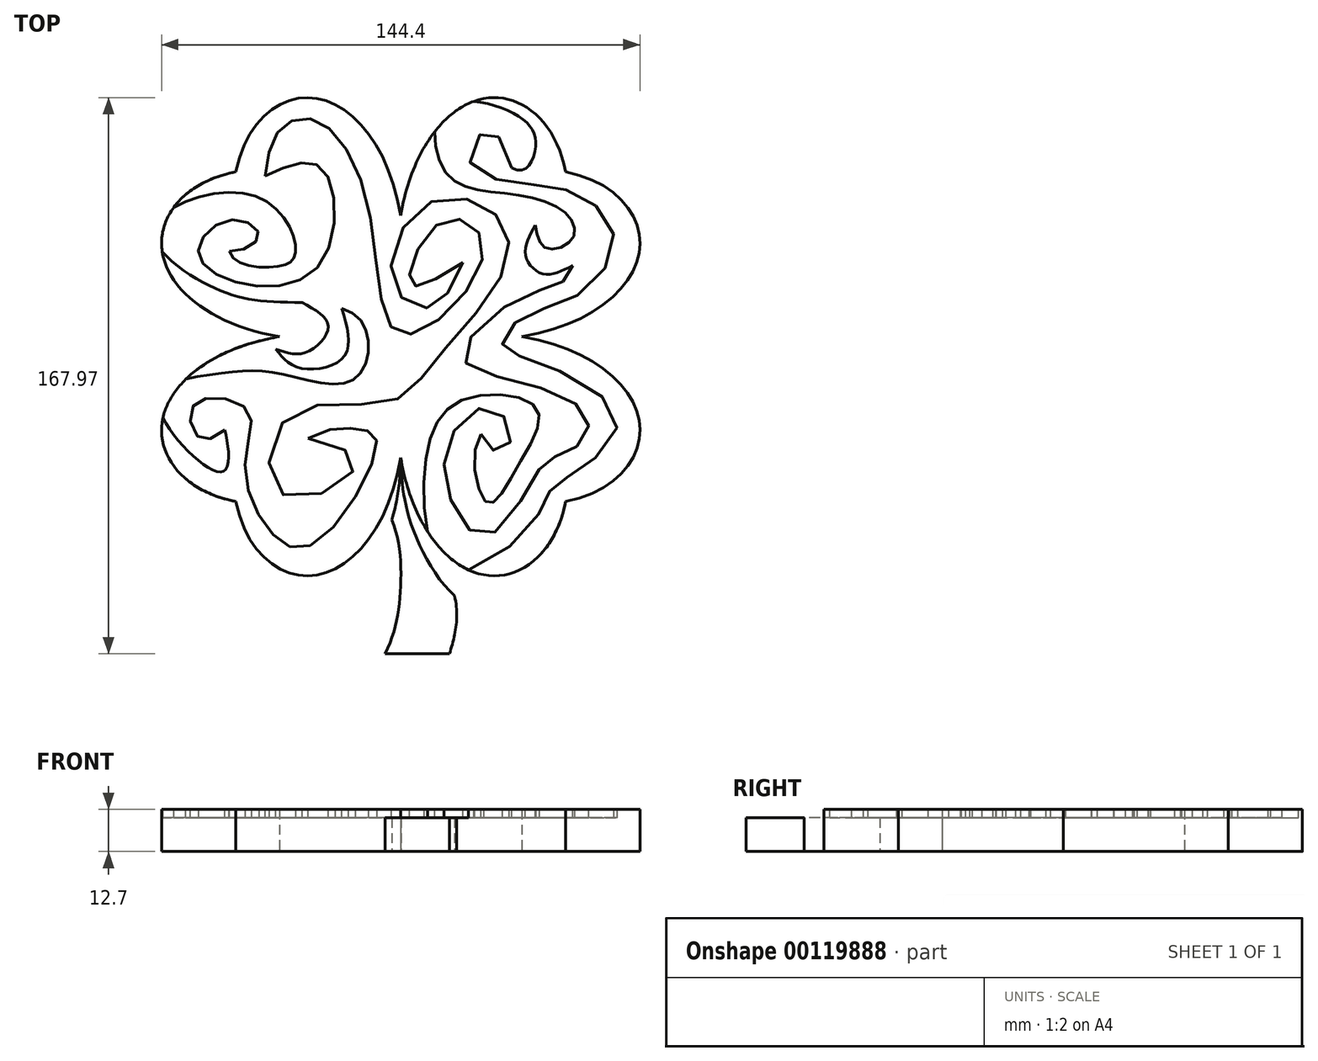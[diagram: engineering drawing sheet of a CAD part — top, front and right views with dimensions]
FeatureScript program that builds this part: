
annotation { "Feature Type Name" : "Feature", "Feature Type Description" : "" }
export const myFeature = defineFeature(function(context is Context, id is Id, definition is map)
    precondition{}
    {
        {
            var Q0;
            Q0=qCreatedBy(makeId("Top.planeOp"),FACE);
            var sketch = newSketch(context, id + "F0", { "sketchPlane" : qUnion([Q0])});
            skLineSegment(sketch, "E0", {"start": v(0, 0) * mm, "end": v(-53.24, 53.24) * mm, "construction": true});
            skFitSpline(sketch, "E1", {"points": [v(-36.57, 0) * mm, v(-72.1, 26.37) * mm, v(-49.78, 49.78) * mm], "startDerivative": vector(-116.66, 19.41) * mm, "endDerivative": vector(102.08, 20.22) * mm});
            skLineSegment(sketch, "E2", {"start": v(-36.57, 0) * mm, "end": v(0, 0) * mm});
            skLineSegment(sketch, "E3", {"start": v(-49.78, 49.78) * mm, "end": v(0, 0) * mm});
            skSolve(sketch);
        }
        {
            var Q0;
            Q0=makeQuery(id+"F0.imprint","IMPRINT",FACE,{"disambiguationData":[TD([[makeQuery(id+"F0.imprint","IMPRINT",EDGE,{"derivedFrom":sQuery(id+"F0.wireOp",EDGE,"E1")}),-1.0]])]});
            extrude(context, id + "F1", {"entities" : qUnion([Q0]), "depth" : 12.7 * mm});
        }
        {
            var Q0;
            Q0=makeQuery(id+"F1.opExtrude","SWEPT_BODY",BODY,{"disambiguationData":[OSD([sQuery(id+"F0.wireOp",EDGE,"E1"),sQuery(id+"F0.wireOp",EDGE,"E2"),sQuery(id+"F0.wireOp",EDGE,"E3")])]});
            var Q1;
            Q1=makeQuery(id+"F1.opExtrude","SWEPT_FACE",FACE,{"disambiguationData":[OSD([sQuery(id+"F0.wireOp",EDGE,"E3")])]});
            mirror(context, id + "F2", {"operationType" : NewBodyOperationType.ADD, "entities" : qUnion([Q0]), "mirrorPlane" : qUnion([Q1])});
        }
        {
            var Q0;
            Q0=qCreatedBy(makeId("Front.planeOp"),FACE);
            var sketch = newSketch(context, id + "F3", { "sketchPlane" : qUnion([Q0])});
            skLineSegment(sketch, "E4", {"start": v(0, 0) * mm, "end": v(0, 34.53) * mm, "construction": true});
            skSolve(sketch);
        }
        {
            var Q0;
            Q0=makeQuery(id+"F1.opExtrude","SWEPT_BODY",BODY,{"disambiguationData":[OSD([sQuery(id+"F0.wireOp",EDGE,"E1"),sQuery(id+"F0.wireOp",EDGE,"E2"),sQuery(id+"F0.wireOp",EDGE,"E3")])]});
            var Q1;
            Q1=sQuery(id+"F3.wireOp",EDGE,"E4");
            circularPattern(context, id + "F4", {"operationType" : NewBodyOperationType.ADD, "entities" : qUnion([Q0]), "axis" : qUnion([Q1]), "angle" : 90 * degree, "instanceCount" : 4});
        }
        {
            var Q0;
            Q0=qCreatedBy(makeId("Top.planeOp"),FACE);
            var sketch = newSketch(context, id + "F5", { "sketchPlane" : qUnion([Q0])});
            skFitSpline(sketch, "E5.0", {"points": [v(0, -36.57) * mm, v(-3.49, -57.53) * mm, v(-24.28, -82.21) * mm, v(-46.67, -65.46) * mm, v(-49.78, -49.78) * mm]});
            skFitSpline(sketch, "E5.1", {"points": [v(0, -36.57) * mm, v(3.49, -57.53) * mm, v(24.28, -82.21) * mm, v(46.67, -65.46) * mm, v(49.78, -49.78) * mm]});
            skFitSpline(sketch, "E6", {"points": [v(-4.48, -52.04) * mm, v(0, -74.63) * mm, v(-4.68, -95.77) * mm], "startDerivative": vector(24.32, -37.72) * mm, "endDerivative": vector(-20.4, -41.32) * mm});
            skFitSpline(sketch, "E7", {"points": [v(8.97, -60.15) * mm, v(16.79, -81.53) * mm, v(14.75, -95.77) * mm], "startDerivative": vector(19.2, -40.12) * mm, "endDerivative": vector(-8.71, -30.77) * mm});
            skLineSegment(sketch, "E8", {"start": v(-4.68, -95.77) * mm, "end": v(14.75, -95.77) * mm});
            skSolve(sketch);
        }
        {
            var Q0;
            Q0 = qSketchRegion(id + "F5", true);
            extrude(context, id + "F6", {"entities" : qUnion([Q0]), "operationType" : NewBodyOperationType.ADD, "depth" : 10.16 * mm});
        }
        {
            var Q0;
            {var subQ0=makeQuery(id+"F1.opExtrude","CAP_FACE",FACE,{"disambiguationData":[OSD([sQuery(id+"F0.wireOp",EDGE,"E1"),sQuery(id+"F0.wireOp",EDGE,"E2"),sQuery(id+"F0.wireOp",EDGE,"E3")])],"isStart":false});var subQ1=makeQuery(id+"F2.boolean.opBoolean","MERGE",FACE,{"derivedFrom":[subQ0,makeQuery(id+"F2.opPattern","COPY",FACE,{"derivedFrom":subQ0,"instanceName":"1"})]});Q0=makeQuery(id+"F4.boolean.opBoolean","MERGE",FACE,{"derivedFrom":[subQ1,makeQuery(id+"F4.opPattern","COPY",FACE,{"derivedFrom":subQ1,"instanceName":"1"}),makeQuery(id+"F4.opPattern","COPY",FACE,{"derivedFrom":subQ1,"instanceName":"2"}),makeQuery(id+"F4.opPattern","COPY",FACE,{"derivedFrom":subQ1,"instanceName":"3"})]});}
            var sketch = newSketch(context, id + "F7", { "sketchPlane" : qUnion([Q0])});
            skFitSpline(sketch, "E9", {"points": [v(-40.9, 48.57) * mm, v(-35.52, 63.52) * mm, v(-24.6, 64.88) * mm, v(-9.32, 37.1) * mm, v(0.62, 0.67) * mm, v(24.97, 25.86) * mm, v(13.1, 35.07) * mm, v(2.91, 16.22) * mm, v(18.71, 22.32) * mm], "startDerivative": vector(11.66, 166.66) * mm, "endDerivative": vector(198.26, 125.29) * mm});
            skFitSpline(sketch, "E10", {"points": [v(18.71, 22.32) * mm, v(9.03, 8.82) * mm, v(-2.18, 15.7) * mm, v(6.54, 39.33) * mm, v(27.1, 38.27) * mm, v(31.88, 22.01) * mm, v(11.1, -6.4) * mm, v(-3.88, -19.8) * mm, v(-34.23, -24.37) * mm, v(-35.52, -47.74) * mm, v(-13.9, -39.6) * mm, v(-27.92, -30.66) * mm], "startDerivative": vector(-99.1, -230.21) * mm, "endDerivative": vector(-297.24, 42.86) * mm});
            skFitSpline(sketch, "E11", {"points": [v(-27.92, -30.66) * mm, v(-12.63, -27.86) * mm, v(-7.25, -31.8) * mm, v(-26.26, -62.6) * mm, v(-39.06, -59.2) * mm, v(-47.02, -38.18) * mm, v(-45.75, -22.9) * mm, v(-57.21, -18.44) * mm, v(-63.46, -22.55) * mm, v(-60.58, -30.66) * mm, v(-53.16, -28.15) * mm], "startDerivative": vector(147.88, 96.46) * mm, "endDerivative": vector(99.72, 79.17) * mm});
            skFitSpline(sketch, "E12", {"points": [v(-53.16, -28.15) * mm, v(-53.16, -40.4) * mm, v(-64.95, -33.8) * mm, v(-72.55, -17.34) * mm, v(-54.67, -11.12) * mm, v(-36.52, -11.12) * mm, v(-13.91, -12.7) * mm, v(-12, 4.8) * mm, v(-37.47, 10.53) * mm, v(-58.8, 15.95) * mm, v(-74.31, 32.92) * mm, v(-43.88, 42.48) * mm, v(-31.74, 25.5) * mm, v(-37.08, 21.22) * mm, v(-51.67, 25.78) * mm], "startDerivative": vector(58.4, -215.03) * mm, "endDerivative": vector(-46.14, 219.1) * mm});
            skFitSpline(sketch, "E13", {"points": [v(-51.67, 25.78) * mm, v(-42.9, 30.38) * mm, v(-51.08, 35.29) * mm, v(-61.15, 25.78) * mm, v(-47.89, 16.02) * mm, v(-23.64, 22.87) * mm, v(-24.08, 51.08) * mm, v(-40.9, 48.57) * mm], "startDerivative": vector(87.66, -14.46) * mm, "endDerivative": vector(-122.16, -56.83) * mm});
            skFitSpline(sketch, "E14", {"points": [v(-29.78, 10.3) * mm, v(-21.9, 3.24) * mm, v(-28.4, -4.66) * mm, v(-37.7, -3.78) * mm], "startDerivative": vector(33.75, -18.1) * mm, "endDerivative": vector(-28.71, 9.75) * mm});
            skFitSpline(sketch, "E15", {"points": [v(-37.7, -3.78) * mm, v(-30.68, -9.4) * mm, v(-17.16, -6.06) * mm, v(-17.74, 8.55) * mm], "startDerivative": vector(19.15, -24.95) * mm, "endDerivative": vector(-13.36, 46.68) * mm});
            skFitSpline(sketch, "E16", {"points": [v(24.27, -29.4) * mm, v(25.93, -50.05) * mm, v(34.75, -40.06) * mm, v(41, -21.68) * mm, v(19.12, -18.92) * mm, v(7.36, -38.78) * mm, v(15.3, -70.35) * mm, v(40.35, -55.65) * mm, v(45.39, -46) * mm, v(53.87, -40.25) * mm, v(65.27, -24.62) * mm, v(40.26, -7.34) * mm, v(30.7, -2.56) * mm, v(36.59, 5.71) * mm, v(54.04, 12.93) * mm, v(64.37, 30.35) * mm, v(52.97, 43.26) * mm, v(35.98, 46.27) * mm, v(20.7, 53.36) * mm, v(26.94, 62.61) * mm, v(33.55, 50.9) * mm], "startDerivative": vector(-225.7, -273.37) * mm, "endDerivative": vector(163.48, -309.4) * mm});
            skFitSpline(sketch, "E17", {"points": [v(33.55, 50.9) * mm, v(40.68, 57.08) * mm, v(35.29, 66.7) * mm, v(13.2, 69.03) * mm, v(13.86, 49.2) * mm, v(32.27, 43.21) * mm, v(50.23, 36.93) * mm, v(51.73, 29.44) * mm, v(43.8, 26.75) * mm, v(40.65, 33.63) * mm], "startDerivative": vector(143.88, -78.9) * mm, "endDerivative": vector(-16.62, 100.05) * mm});
            skFitSpline(sketch, "E18", {"points": [v(40.65, 33.63) * mm, v(37.66, 24.65) * mm, v(43.05, 18.96) * mm, v(51.88, 21.5) * mm], "startDerivative": vector(-15.25, -26.49) * mm, "endDerivative": vector(26.68, 14.01) * mm});
            skFitSpline(sketch, "E19", {"points": [v(51.88, 21.5) * mm, v(48.85, 16.57) * mm, v(35.71, 11.63) * mm, v(18.82, -6.1) * mm, v(36.54, -13.8) * mm, v(55.96, -23.65) * mm, v(54.53, -31.96) * mm, v(45.9, -36.48) * mm, v(40.66, -41.95) * mm, v(26.1, -60.16) * mm, v(15.35, -50.04) * mm, v(15.09, -30.36) * mm, v(27.28, -21.38) * mm, v(33.37, -31.04) * mm, v(28.3, -34.42) * mm, v(24.27, -29.4) * mm], "startDerivative": vector(-47.03, -125.61) * mm, "endDerivative": vector(-67.2, 145.56) * mm});
            skSolve(sketch);
        }
        {
            var Q0;
            Q0 = qSketchRegion(id + "F7", true);
            extrude(context, id + "F8", {"entities" : qUnion([Q0]), "operationType" : NewBodyOperationType.REMOVE, "oppositeDirection" : true, "depth" : 2.54 * mm});
        }
    });
